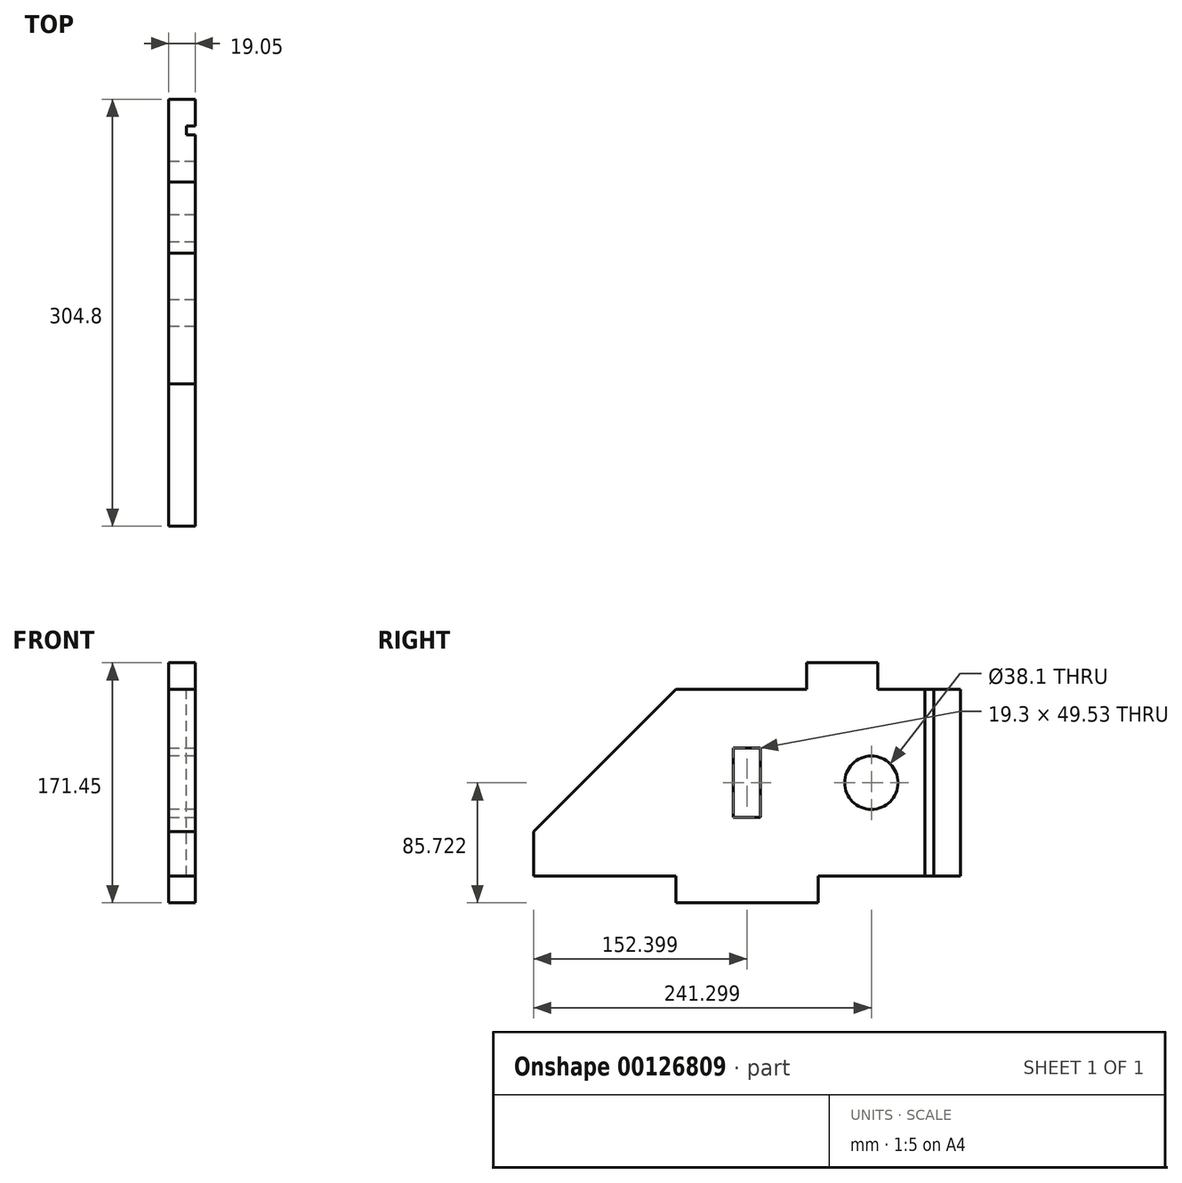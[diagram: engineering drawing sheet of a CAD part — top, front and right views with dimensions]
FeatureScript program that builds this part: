
annotation { "Feature Type Name" : "Feature", "Feature Type Description" : "" }
export const myFeature = defineFeature(function(context is Context, id is Id, definition is map)
    precondition{}
    {
        {
            var Q0;
            Q0=qCreatedBy(makeId("Right.planeOp"),FACE);
            var sketch = newSketch(context, id + "F0", { "sketchPlane" : qUnion([Q0])});
            skLineSegment(sketch, "E0.bottom", {"start": v(-248.57, -19.5) * mm, "end": v(56.23, -19.5) * mm});
            skLineSegment(sketch, "E0.top", {"start": v(-248.57, -171.9) * mm, "end": v(56.23, -171.9) * mm});
            skLineSegment(sketch, "E0.left", {"start": v(-248.57, -19.5) * mm, "end": v(-248.57, -171.9) * mm});
            skLineSegment(sketch, "E0.right", {"start": v(56.23, -19.5) * mm, "end": v(56.23, -171.9) * mm});
            skSolve(sketch);
        }
        {
            var Q0;
            Q0=qSketchRegion(id+"F0",true);
            extrude(context, id + "F1", {"entities" : qUnion([Q0]), "depth" : 19.05 * mm});
        }
        {
            var Q0;
            Q0=makeQuery(id+"F1.opExtrude","CAP_FACE",FACE,{"disambiguationData":[OSD([sQuery(id+"F0.wireOp",EDGE,"E0.bottom"),sQuery(id+"F0.wireOp",EDGE,"E0.top"),sQuery(id+"F0.wireOp",EDGE,"E0.left"),sQuery(id+"F0.wireOp",EDGE,"E0.right")])],"isStart":false});
            var sketch = newSketch(context, id + "F2", { "sketchPlane" : qUnion([Q0])});
            skLineSegment(sketch, "E1.bottom", {"start": v(-248.57, -171.9) * mm, "end": v(-146.97, -171.9) * mm});
            skLineSegment(sketch, "E1.top", {"start": v(-248.57, -152.85) * mm, "end": v(-146.97, -152.85) * mm});
            skLineSegment(sketch, "E1.left", {"start": v(-248.57, -171.9) * mm, "end": v(-248.57, -152.85) * mm});
            skLineSegment(sketch, "E1.right", {"start": v(-146.97, -171.9) * mm, "end": v(-146.97, -152.85) * mm});
            skLineSegment(sketch, "E2.bottom", {"start": v(56.23, -171.9) * mm, "end": v(-45.37, -171.9) * mm});
            skLineSegment(sketch, "E2.top", {"start": v(56.23, -152.85) * mm, "end": v(-45.37, -152.85) * mm});
            skLineSegment(sketch, "E2.left", {"start": v(56.23, -171.9) * mm, "end": v(56.23, -152.85) * mm});
            skLineSegment(sketch, "E2.right", {"start": v(-45.37, -171.9) * mm, "end": v(-45.37, -152.85) * mm});
            skLineSegment(sketch, "E3", {"start": v(-146.97, -171.9) * mm, "end": v(-45.37, -171.9) * mm});
            skSolve(sketch);
        }
        {
            var Q0;
            Q0=qSketchRegion(id+"F2",true);
            extrude(context, id + "F3", {"entities" : qUnion([Q0]), "operationType" : NewBodyOperationType.REMOVE, "endBound" : BoundingType.THROUGH_ALL, "oppositeDirection" : true, "depth" : 25.4 * mm});
        }
        {
            var Q0;
            Q0=makeQuery(id+"F1.opExtrude","CAP_FACE",FACE,{"disambiguationData":[OSD([sQuery(id+"F0.wireOp",EDGE,"E0.bottom"),sQuery(id+"F0.wireOp",EDGE,"E0.top"),sQuery(id+"F0.wireOp",EDGE,"E0.left"),sQuery(id+"F0.wireOp",EDGE,"E0.right")])],"isStart":false});
            var sketch = newSketch(context, id + "F4", { "sketchPlane" : qUnion([Q0])});
            skLineSegment(sketch, "E4", {"start": v(-146.97, -152.85) * mm, "end": v(-45.37, -152.85) * mm});
            skLineSegment(sketch, "E5.0", {"start": v(-86.52, -110.94) * mm, "end": v(-86.52, -61.41) * mm});
            skLineSegment(sketch, "E6.0", {"start": v(-105.82, -110.94) * mm, "end": v(-105.82, -61.41) * mm});
            skLineSegment(sketch, "E7.0", {"start": v(-105.82, -61.41) * mm, "end": v(-86.52, -61.41) * mm});
            skLineSegment(sketch, "E8.0", {"start": v(-105.82, -110.94) * mm, "end": v(-86.52, -110.94) * mm});
            skSolve(sketch);
        }
        {
            var Q0;
            Q0=qSketchRegion(id+"F4",true);
            extrude(context, id + "F5", {"entities" : qUnion([Q0]), "operationType" : NewBodyOperationType.REMOVE, "endBound" : BoundingType.THROUGH_ALL, "oppositeDirection" : true, "depth" : 25.4 * mm});
        }
        {
            var Q0;
            Q0=makeQuery(id+"F1.opExtrude","SWEPT_FACE",FACE,{"disambiguationData":[OSD([sQuery(id+"F0.wireOp",EDGE,"E0.bottom")])]});
            var sketch = newSketch(context, id + "F6", { "sketchPlane" : qUnion([Q0])});
            skLineSegment(sketch, "E9.0", {"start": v(12.7, 37.18) * mm, "end": v(12.7, 30.83) * mm});
            skLineSegment(sketch, "E10.bottom", {"start": v(12.7, 37.18) * mm, "end": v(19.05, 37.18) * mm});
            skLineSegment(sketch, "E10.top", {"start": v(12.7, 30.83) * mm, "end": v(19.05, 30.83) * mm});
            skLineSegment(sketch, "E10.right", {"start": v(19.05, 37.18) * mm, "end": v(19.05, 30.83) * mm});
            skSolve(sketch);
        }
        {
            var Q0;
            Q0=qSketchRegion(id+"F6",true);
            extrude(context, id + "F7", {"entities" : qUnion([Q0]), "operationType" : NewBodyOperationType.REMOVE, "endBound" : BoundingType.THROUGH_ALL, "oppositeDirection" : true, "depth" : 158 * mm});
        }
        {
            var Q0;
            {var subQ0=sQuery(id+"F0.wireOp",EDGE,"E0.bottom");var subQ1=sQuery(id+"F0.wireOp",EDGE,"E0.top");var subQ2=sQuery(id+"F0.wireOp",EDGE,"E0.left");Q0=makeQuery(id+"F7.boolean.opBoolean","SPLIT",FACE,{"disambiguationData":[TD([makeQuery(id+"F1.opExtrude","SWEPT_FACE",FACE,{"disambiguationData":[OSD([subQ1])]})])],"derivedFrom":makeQuery(id+"F1.opExtrude","CAP_FACE",FACE,{"disambiguationData":[OSD([subQ0,subQ1,subQ2,sQuery(id+"F0.wireOp",EDGE,"E0.right")])],"isStart":false})});}
            var sketch = newSketch(context, id + "F8", { "sketchPlane" : qUnion([Q0])});
            skLineSegment(sketch, "E11", {"start": v(-248.57, -19.5) * mm, "end": v(-146.97, -19.5) * mm});
            skLineSegment(sketch, "E12", {"start": v(-248.57, -19.5) * mm, "end": v(-248.57, -121.1) * mm});
            skLineSegment(sketch, "E13", {"start": v(-248.57, -121.1) * mm, "end": v(-146.97, -19.5) * mm});
            skSolve(sketch);
        }
        {
            var Q0;
            Q0 = qSketchRegion(id + "F8", true);
            extrude(context, id + "F9", {"entities" : qUnion([Q0]), "operationType" : NewBodyOperationType.REMOVE, "endBound" : BoundingType.THROUGH_ALL, "oppositeDirection" : true, "depth" : 25.4 * mm});
        }
        {
            var Q0;
            Q0=makeQuery(id+"F1.opExtrude","CAP_FACE",FACE,{"disambiguationData":[OSD([sQuery(id+"F0.wireOp",EDGE,"E0.bottom"),sQuery(id+"F0.wireOp",EDGE,"E0.top"),sQuery(id+"F0.wireOp",EDGE,"E0.left"),sQuery(id+"F0.wireOp",EDGE,"E0.right")])],"isStart":true});
            var sketch = newSketch(context, id + "F10", { "sketchPlane" : qUnion([Q0])});
            skCircle(sketch, "E14", {"center": v(7.27, -86.18) * mm, "radius": 19.05 * mm});
            skSolve(sketch);
        }
        {
            var Q0;
            Q0 = qSketchRegion(id + "F10", true);
            extrude(context, id + "F11", {"entities" : qUnion([Q0]), "operationType" : NewBodyOperationType.REMOVE, "endBound" : BoundingType.THROUGH_ALL, "oppositeDirection" : true, "depth" : 25.4 * mm});
        }
        {
            var Q0;
            {var subQ0=sQuery(id+"F0.wireOp",EDGE,"E0.bottom");var subQ1=sQuery(id+"F0.wireOp",EDGE,"E0.top");var subQ2=sQuery(id+"F0.wireOp",EDGE,"E0.left");Q0=makeQuery(id+"F7.boolean.opBoolean","SPLIT",FACE,{"disambiguationData":[TD([makeQuery(id+"F1.opExtrude","SWEPT_FACE",FACE,{"disambiguationData":[OSD([subQ1])]})])],"derivedFrom":makeQuery(id+"F1.opExtrude","CAP_FACE",FACE,{"disambiguationData":[OSD([subQ0,subQ1,subQ2,sQuery(id+"F0.wireOp",EDGE,"E0.right")])],"isStart":false})});}
            var sketch = newSketch(context, id + "F12", { "sketchPlane" : qUnion([Q0])});
            skLineSegment(sketch, "E15", {"start": v(-86.52, -19.5) * mm, "end": v(-53.5, -19.5) * mm});
            skLineSegment(sketch, "E16.bottom", {"start": v(-53.5, -19.5) * mm, "end": v(-2.7, -19.5) * mm});
            skLineSegment(sketch, "E16.top", {"start": v(-53.5, -0.45) * mm, "end": v(-2.7, -0.45) * mm});
            skLineSegment(sketch, "E16.left", {"start": v(-53.5, -19.5) * mm, "end": v(-53.5, -0.45) * mm});
            skLineSegment(sketch, "E16.right", {"start": v(-2.7, -19.5) * mm, "end": v(-2.7, -0.45) * mm});
            skSolve(sketch);
        }
        {
            var Q0;
            Q0 = qSketchRegion(id + "F12", true);
            extrude(context, id + "F13", {"entities" : qUnion([Q0]), "operationType" : NewBodyOperationType.ADD, "oppositeDirection" : true, "depth" : 19.05 * mm});
        }
    });
